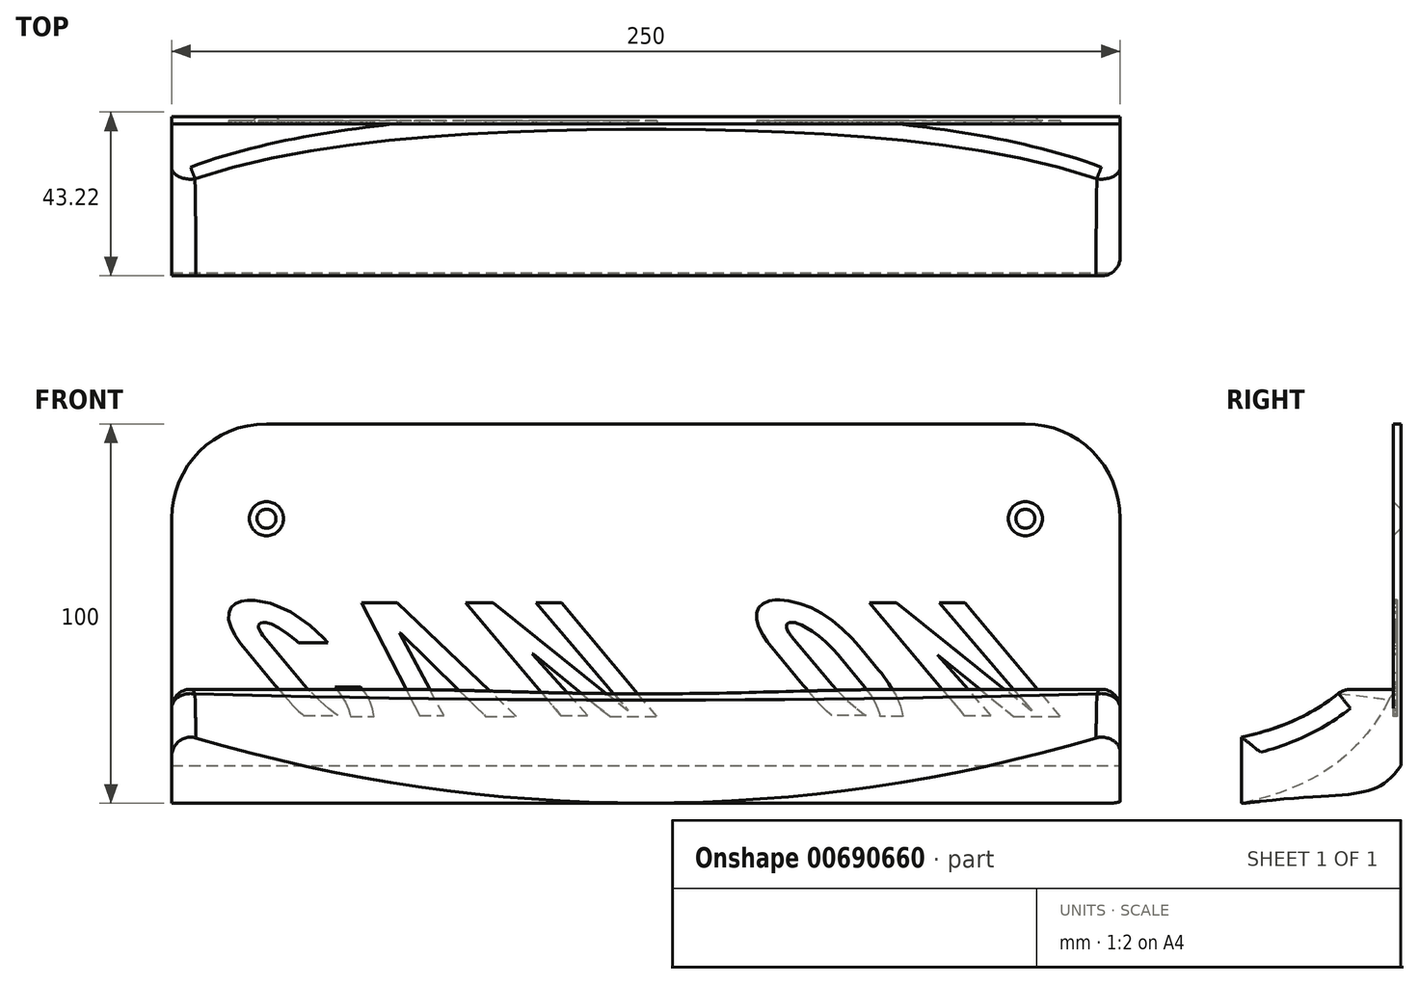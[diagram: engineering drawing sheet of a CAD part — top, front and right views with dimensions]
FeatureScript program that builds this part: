
annotation { "Feature Type Name" : "Feature", "Feature Type Description" : "" }
export const myFeature = defineFeature(function(context is Context, id is Id, definition is map)
    precondition{}
    {
        {
            assignVariable(context, id + "F0", {"name" : "raddurchmesser", "anyValue" : 736});
        }
        {
            var Q0;
            Q0=qCreatedBy(makeId("Front.planeOp"),FACE);
            var sketch = newSketch(context, id + "F1", { "sketchPlane" : qUnion([Q0])});
            skLineSegment(sketch, "E0.bottom", {"start": v(125, -50) * mm, "end": v(-125, -50) * mm});
            skLineSegment(sketch, "E0.top", {"start": v(100, 50) * mm, "end": v(-100, 50) * mm});
            skLineSegment(sketch, "E0.left", {"start": v(125, -50) * mm, "end": v(125, 25) * mm});
            skLineSegment(sketch, "E0.right", {"start": v(-125, -50) * mm, "end": v(-125, 25) * mm});
            skPoint(sketch, "E0.middle", {"position": v(0, 0) * mm});
            skPoint(sketch, "E1.visualSharp", {"position": v(-125, 50) * mm});
            skArc(sketch, "E1.filletArc", {"start": v(-100, 50) * mm, "mid": v(-117.68, 42.68) * mm, "end": v(-125, 25) * mm});
            skPoint(sketch, "E2.visualSharp", {"position": v(125, 50) * mm});
            skArc(sketch, "E2.filletArc", {"start": v(125, 25) * mm, "mid": v(117.68, 42.68) * mm, "end": v(100, 50) * mm});
            skSolve(sketch);
        }
        {
            var Q0;
            Q0=makeQuery(id+"F1.imprint","IMPRINT",FACE,{"disambiguationData":[TD([[makeQuery(id+"F1.imprint","IMPRINT",EDGE,{"derivedFrom":sQuery(id+"F1.wireOp",EDGE,"E0.bottom")}),-1.0]])]});
            extrude(context, id + "F2", {"entities" : qUnion([Q0]), "depth" : 2 * mm, "offsetDistance" : 25 * mm});
        }
        {
            var Q0;
            Q0=makeQuery(id+"F2.opExtrude","CAP_FACE",FACE,{"disambiguationData":[OSD([sQuery(id+"F1.wireOp",EDGE,"E0.bottom"),sQuery(id+"F1.wireOp",EDGE,"E0.top"),sQuery(id+"F1.wireOp",EDGE,"E0.left"),sQuery(id+"F1.wireOp",EDGE,"E0.right"),sQuery(id+"F1.wireOp",EDGE,"E1.filletArc"),sQuery(id+"F1.wireOp",EDGE,"E2.filletArc")])],"isStart":false});
            var sketch = newSketch(context, id + "F3", { "sketchPlane" : qUnion([Q0])});
            skPoint(sketch, "E3", {"position": v(-100, 25) * mm});
            skPoint(sketch, "E4", {"position": v(100, 25) * mm});
            skSolve(sketch);
        }
        {
            var Q0;
            Q0=sQuery(id+"F3.wireOp",VERTEX,"E3");
            var Q1;
            Q1=sQuery(id+"F3.wireOp",VERTEX,"E4");
            var Q2;
            Q2=makeQuery(id+"F2.opExtrude","SWEPT_BODY",BODY,{"disambiguationData":[OSD([sQuery(id+"F1.wireOp",EDGE,"E0.bottom"),sQuery(id+"F1.wireOp",EDGE,"E0.top"),sQuery(id+"F1.wireOp",EDGE,"E0.left"),sQuery(id+"F1.wireOp",EDGE,"E0.right"),sQuery(id+"F1.wireOp",EDGE,"E1.filletArc"),sQuery(id+"F1.wireOp",EDGE,"E2.filletArc")])]});
            hole(context, id + "F4", {"style" : HoleStyle.C_SINK, "endStyle" : HoleEndStyle.THROUGH, "holeDiameter" : 4 * mm, "cSinkDiameter" : 9 * mm, "cSinkAngle" : 90 * degree, "majorDiameter" : 5 * mm, "isTappedThrough" : true, "tappedDepth" : 12 * mm, "tapClearance" : 3, "locations" : qUnion([Q0, Q1]), "scope" : qUnion([Q2])});
        }
        {
            var Q0;
            Q0=makeQuery(id+"F2.opExtrude","CAP_FACE",FACE,{"disambiguationData":[OSD([sQuery(id+"F1.wireOp",EDGE,"E0.bottom"),sQuery(id+"F1.wireOp",EDGE,"E0.top"),sQuery(id+"F1.wireOp",EDGE,"E0.left"),sQuery(id+"F1.wireOp",EDGE,"E0.right")])],"isStart":false});
            var sketch = newSketch(context, id + "F5", { "sketchPlane" : qUnion([Q0])});
            skLineSegment(sketch, "E5.bottom", {"start": v(-125, -50) * mm, "end": v(125, -50) * mm});
            skLineSegment(sketch, "E5.top", {"start": v(-125, -20) * mm, "end": v(125, -20) * mm});
            skLineSegment(sketch, "E5.left", {"start": v(-125, -50) * mm, "end": v(-125, -20) * mm});
            skLineSegment(sketch, "E5.right", {"start": v(125, -50) * mm, "end": v(125, -20) * mm});
            skSolve(sketch);
        }
        {
            var Q0;
            Q0=makeQuery(id+"F5.imprint","IMPRINT",FACE,{"disambiguationData":[TD([[makeQuery(id+"F5.imprint","IMPRINT",EDGE,{"derivedFrom":sQuery(id+"F5.wireOp",EDGE,"E5.bottom")}),-1.0]])]});
            extrude(context, id + "F6", {"entities" : qUnion([Q0]), "operationType" : NewBodyOperationType.ADD, "depth" : 40 * mm, "offsetDistance" : 25 * mm});
        }
        {
            var Q0;
            Q0=makeQuery(id+"F2.opExtrude","CAP_FACE",FACE,{"disambiguationData":[OSD([sQuery(id+"F1.wireOp",EDGE,"E0.bottom"),sQuery(id+"F1.wireOp",EDGE,"E0.top"),sQuery(id+"F1.wireOp",EDGE,"E0.left"),sQuery(id+"F1.wireOp",EDGE,"E0.right"),sQuery(id+"F1.wireOp",EDGE,"E1.filletArc"),sQuery(id+"F1.wireOp",EDGE,"E2.filletArc")])],"isStart":false});
            var sketch = newSketch(context, id + "F7", { "sketchPlane" : qUnion([Q0])});
            skLineSegment(sketch, "E6", {"start": v(-104.56, 3.5) * mm, "end": v(-105.1, 3.5) * mm});
            skLineSegment(sketch, "E7", {"start": v(-105.1, 3.5) * mm, "end": v(-106.67, 3.27) * mm});
            skLineSegment(sketch, "E8", {"start": v(-106.67, 3.27) * mm, "end": v(-108.27, 2.6) * mm});
            skLineSegment(sketch, "E9", {"start": v(-108.27, 2.6) * mm, "end": v(-109.36, 1.52) * mm});
            skLineSegment(sketch, "E10", {"start": v(-109.36, 1.52) * mm, "end": v(-109.92, 0.11) * mm});
            skLineSegment(sketch, "E11", {"start": v(-109.92, 0.11) * mm, "end": v(-109.94, -1.6) * mm});
            skLineSegment(sketch, "E12", {"start": v(-109.94, -1.6) * mm, "end": v(-109.4, -3.57) * mm});
            skLineSegment(sketch, "E13", {"start": v(-109.4, -3.57) * mm, "end": v(-108.31, -5.75) * mm});
            skLineSegment(sketch, "E14", {"start": v(-108.31, -5.75) * mm, "end": v(-107.09, -7.53) * mm});
            skLineSegment(sketch, "E15", {"start": v(-107.09, -7.53) * mm, "end": v(-106.63, -8.08) * mm});
            skLineSegment(sketch, "E16", {"start": v(-106.63, -8.08) * mm, "end": v(-97.74, -18.87) * mm});
            skLineSegment(sketch, "E17", {"start": v(-97.74, -18.87) * mm, "end": v(-97.17, -19.56) * mm});
            skLineSegment(sketch, "E18", {"start": v(-97.17, -19.56) * mm, "end": v(-95.4, -21.6) * mm});
            skLineSegment(sketch, "E19", {"start": v(-95.4, -21.6) * mm, "end": v(-93.3, -23.92) * mm});
            skLineSegment(sketch, "E20", {"start": v(-93.3, -23.92) * mm, "end": v(-91.54, -25.7) * mm});
            skLineSegment(sketch, "E21", {"start": v(-91.54, -25.7) * mm, "end": v(-90.6, -26.57) * mm});
            skLineSegment(sketch, "E22", {"start": v(-90.6, -26.57) * mm, "end": v(-90.28, -26.83) * mm});
            skLineSegment(sketch, "E23", {"start": v(-90.28, -26.83) * mm, "end": v(-90.27, -26.84) * mm});
            skLineSegment(sketch, "E24", {"start": v(-90.27, -26.84) * mm, "end": v(-90.18, -26.87) * mm});
            skLineSegment(sketch, "E25", {"start": v(-90.18, -26.87) * mm, "end": v(-90.15, -26.87) * mm});
            skLineSegment(sketch, "E26", {"start": v(-90.15, -26.87) * mm, "end": v(-81.14, -26.87) * mm});
            skLineSegment(sketch, "E27", {"start": v(-81.14, -26.87) * mm, "end": v(-81.77, -26.47) * mm});
            skLineSegment(sketch, "E28", {"start": v(-81.77, -26.47) * mm, "end": v(-83.55, -25.11) * mm});
            skLineSegment(sketch, "E29", {"start": v(-83.55, -25.11) * mm, "end": v(-86.05, -22.95) * mm});
            skLineSegment(sketch, "E30", {"start": v(-86.05, -22.95) * mm, "end": v(-88.48, -20.56) * mm});
            skLineSegment(sketch, "E31", {"start": v(-88.48, -20.56) * mm, "end": v(-90.15, -18.76) * mm});
            skLineSegment(sketch, "E32", {"start": v(-90.15, -18.76) * mm, "end": v(-90.68, -18.14) * mm});
            skLineSegment(sketch, "E33", {"start": v(-90.68, -18.14) * mm, "end": v(-100.73, -6.07) * mm});
            skLineSegment(sketch, "E34", {"start": v(-100.73, -6.07) * mm, "end": v(-100.92, -5.85) * mm});
            skLineSegment(sketch, "E35", {"start": v(-100.92, -5.85) * mm, "end": v(-101.42, -5.15) * mm});
            skLineSegment(sketch, "E36", {"start": v(-101.42, -5.15) * mm, "end": v(-101.88, -4.35) * mm});
            skLineSegment(sketch, "E37", {"start": v(-101.88, -4.35) * mm, "end": v(-102.1, -3.68) * mm});
            skLineSegment(sketch, "E38", {"start": v(-102.1, -3.68) * mm, "end": v(-102.12, -3.14) * mm});
            skLineSegment(sketch, "E39", {"start": v(-102.12, -3.14) * mm, "end": v(-101.91, -2.73) * mm});
            skLineSegment(sketch, "E40", {"start": v(-101.91, -2.73) * mm, "end": v(-101.5, -2.47) * mm});
            skLineSegment(sketch, "E41", {"start": v(-101.5, -2.47) * mm, "end": v(-100.87, -2.37) * mm});
            skLineSegment(sketch, "E42", {"start": v(-100.87, -2.37) * mm, "end": v(-100.24, -2.38) * mm});
            skLineSegment(sketch, "E43", {"start": v(-100.24, -2.38) * mm, "end": v(-100.04, -2.41) * mm});
            skLineSegment(sketch, "E44", {"start": v(-100.04, -2.41) * mm, "end": v(-99.72, -2.45) * mm});
            skLineSegment(sketch, "E45", {"start": v(-99.72, -2.45) * mm, "end": v(-98.72, -2.83) * mm});
            skLineSegment(sketch, "E46", {"start": v(-98.72, -2.83) * mm, "end": v(-96.75, -3.83) * mm});
            skLineSegment(sketch, "E47", {"start": v(-96.75, -3.83) * mm, "end": v(-94.3, -5.45) * mm});
            skLineSegment(sketch, "E48", {"start": v(-94.3, -5.45) * mm, "end": v(-92.22, -7.13) * mm});
            skLineSegment(sketch, "E49", {"start": v(-92.22, -7.13) * mm, "end": v(-91.57, -7.73) * mm});
            skLineSegment(sketch, "E50", {"start": v(-91.57, -7.73) * mm, "end": v(-83.82, -7.73) * mm});
            skLineSegment(sketch, "E51", {"start": v(-83.82, -7.73) * mm, "end": v(-84.92, -6.5) * mm});
            skLineSegment(sketch, "E52", {"start": v(-84.92, -6.5) * mm, "end": v(-88.54, -3.1) * mm});
            skLineSegment(sketch, "E53", {"start": v(-88.54, -3.1) * mm, "end": v(-93.6, 0.44) * mm});
            skLineSegment(sketch, "E54", {"start": v(-93.6, 0.44) * mm, "end": v(-98.95, 2.7) * mm});
            skLineSegment(sketch, "E55", {"start": v(-98.95, 2.7) * mm, "end": v(-103.16, 3.5) * mm});
            skLineSegment(sketch, "E56", {"start": v(-103.16, 3.5) * mm, "end": v(-104.56, 3.5) * mm});
            skLineSegment(sketch, "E57", {"start": v(-77.84, -27.12) * mm, "end": v(-71.65, -27.12) * mm});
            skLineSegment(sketch, "E58", {"start": v(-71.65, -27.12) * mm, "end": v(-71.7, -26.65) * mm});
            skLineSegment(sketch, "E59", {"start": v(-71.7, -26.65) * mm, "end": v(-72.02, -25.28) * mm});
            skLineSegment(sketch, "E60", {"start": v(-72.02, -25.28) * mm, "end": v(-72.7, -23.34) * mm});
            skLineSegment(sketch, "E61", {"start": v(-72.7, -23.34) * mm, "end": v(-73.73, -21.36) * mm});
            skLineSegment(sketch, "E62", {"start": v(-73.73, -21.36) * mm, "end": v(-74.75, -19.86) * mm});
            skLineSegment(sketch, "E63", {"start": v(-74.75, -19.86) * mm, "end": v(-75.14, -19.4) * mm});
            skLineSegment(sketch, "E64", {"start": v(-75.14, -19.4) * mm, "end": v(-81.95, -19.4) * mm});
            skLineSegment(sketch, "E65", {"start": v(-81.95, -19.4) * mm, "end": v(-81.53, -19.9) * mm});
            skLineSegment(sketch, "E66", {"start": v(-81.53, -19.9) * mm, "end": v(-80.35, -21.5) * mm});
            skLineSegment(sketch, "E67", {"start": v(-80.35, -21.5) * mm, "end": v(-79.19, -23.43) * mm});
            skLineSegment(sketch, "E68", {"start": v(-79.19, -23.43) * mm, "end": v(-78.37, -25.28) * mm});
            skLineSegment(sketch, "E69", {"start": v(-78.37, -25.28) * mm, "end": v(-77.95, -26.65) * mm});
            skLineSegment(sketch, "E70", {"start": v(-77.95, -26.65) * mm, "end": v(-77.84, -27.12) * mm});
            skLineSegment(sketch, "E71", {"start": v(26.03, -18.8) * mm, "end": v(16.1, 2.89) * mm});
            skLineSegment(sketch, "E72", {"start": v(16.1, 2.89) * mm, "end": v(9.93, 2.89) * mm});
            skLineSegment(sketch, "E73", {"start": v(9.93, 2.89) * mm, "end": v(17.34, -11.96) * mm});
            skLineSegment(sketch, "E74", {"start": v(17.34, -11.96) * mm, "end": v(17.13, -11.96) * mm});
            skLineSegment(sketch, "E75", {"start": v(17.13, -11.96) * mm, "end": v(-2.65, 2.89) * mm});
            skLineSegment(sketch, "E76", {"start": v(-2.65, 2.89) * mm, "end": v(-11.42, 2.89) * mm});
            skLineSegment(sketch, "E77", {"start": v(-11.42, 2.89) * mm, "end": v(19.58, -20.05) * mm});
            skLineSegment(sketch, "E78", {"start": v(19.58, -20.05) * mm, "end": v(25.54, -27.11) * mm});
            skLineSegment(sketch, "E79", {"start": v(25.54, -27.11) * mm, "end": v(33.04, -27.11) * mm});
            skLineSegment(sketch, "E80", {"start": v(33.04, -27.11) * mm, "end": v(26.03, -18.8) * mm});
            skLineSegment(sketch, "E81", {"start": v(-28.98, 2.89) * mm, "end": v(-4.66, -25.6) * mm});
            skLineSegment(sketch, "E82", {"start": v(-4.66, -25.6) * mm, "end": v(-4.87, -25.6) * mm});
            skLineSegment(sketch, "E83", {"start": v(-4.87, -25.6) * mm, "end": v(-40.28, 2.89) * mm});
            skLineSegment(sketch, "E84", {"start": v(-40.28, 2.89) * mm, "end": v(-47.46, 2.89) * mm});
            skLineSegment(sketch, "E85", {"start": v(-47.46, 2.89) * mm, "end": v(-22.5, -26.86) * mm});
            skLineSegment(sketch, "E86", {"start": v(-22.5, -26.86) * mm, "end": v(-15.37, -26.86) * mm});
            skLineSegment(sketch, "E87", {"start": v(-15.37, -26.86) * mm, "end": v(-29.96, -10.7) * mm});
            skLineSegment(sketch, "E88", {"start": v(-29.96, -10.7) * mm, "end": v(-29.76, -10.7) * mm});
            skLineSegment(sketch, "E89", {"start": v(-29.76, -10.7) * mm, "end": v(-9.52, -27.11) * mm});
            skLineSegment(sketch, "E90", {"start": v(-9.52, -27.11) * mm, "end": v(2.87, -27.11) * mm});
            skLineSegment(sketch, "E91", {"start": v(2.87, -27.11) * mm, "end": v(-22.3, 2.89) * mm});
            skLineSegment(sketch, "E92", {"start": v(-22.3, 2.89) * mm, "end": v(-28.98, 2.89) * mm});
            skLineSegment(sketch, "E93", {"start": v(77.38, 2.89) * mm, "end": v(101.7, -25.6) * mm});
            skLineSegment(sketch, "E94", {"start": v(101.7, -25.6) * mm, "end": v(101.5, -25.6) * mm});
            skLineSegment(sketch, "E95", {"start": v(101.5, -25.6) * mm, "end": v(66.07, 2.89) * mm});
            skLineSegment(sketch, "E96", {"start": v(66.07, 2.89) * mm, "end": v(58.9, 2.89) * mm});
            skLineSegment(sketch, "E97", {"start": v(58.9, 2.89) * mm, "end": v(83.86, -26.86) * mm});
            skLineSegment(sketch, "E98", {"start": v(83.86, -26.86) * mm, "end": v(90.99, -26.86) * mm});
            skLineSegment(sketch, "E99", {"start": v(90.99, -26.86) * mm, "end": v(76.66, -10.7) * mm});
            skLineSegment(sketch, "E100", {"start": v(76.66, -10.7) * mm, "end": v(76.6, -10.7) * mm});
            skLineSegment(sketch, "E101", {"start": v(76.6, -10.7) * mm, "end": v(96.84, -27.11) * mm});
            skLineSegment(sketch, "E102", {"start": v(96.84, -27.11) * mm, "end": v(109.23, -27.11) * mm});
            skLineSegment(sketch, "E103", {"start": v(109.23, -27.11) * mm, "end": v(84.06, 2.89) * mm});
            skLineSegment(sketch, "E104", {"start": v(84.06, 2.89) * mm, "end": v(77.38, 2.89) * mm});
            skLineSegment(sketch, "E105", {"start": v(-75, 2.89) * mm, "end": v(-59.66, -26.86) * mm});
            skLineSegment(sketch, "E106", {"start": v(-59.66, -26.86) * mm, "end": v(-53.28, -26.86) * mm});
            skLineSegment(sketch, "E107", {"start": v(-53.28, -26.86) * mm, "end": v(-64.91, -5.16) * mm});
            skLineSegment(sketch, "E108", {"start": v(-64.91, -5.16) * mm, "end": v(-64.72, -5.16) * mm});
            skLineSegment(sketch, "E109", {"start": v(-64.72, -5.16) * mm, "end": v(-42.25, -27.11) * mm});
            skLineSegment(sketch, "E110", {"start": v(-42.25, -27.11) * mm, "end": v(-34.2, -27.11) * mm});
            skLineSegment(sketch, "E111", {"start": v(-34.2, -27.11) * mm, "end": v(-65.58, 2.89) * mm});
            skLineSegment(sketch, "E112", {"start": v(-65.58, 2.89) * mm, "end": v(-75, 2.89) * mm});
            skLineSegment(sketch, "E113", {"start": v(48.47, -18.12) * mm, "end": v(49, -18.74) * mm});
            skLineSegment(sketch, "E114", {"start": v(49, -18.74) * mm, "end": v(50.68, -20.55) * mm});
            skLineSegment(sketch, "E115", {"start": v(50.68, -20.55) * mm, "end": v(53.11, -22.94) * mm});
            skLineSegment(sketch, "E116", {"start": v(53.11, -22.94) * mm, "end": v(55.61, -25.1) * mm});
            skLineSegment(sketch, "E117", {"start": v(55.61, -25.1) * mm, "end": v(57.4, -26.46) * mm});
            skLineSegment(sketch, "E118", {"start": v(57.4, -26.46) * mm, "end": v(58.03, -26.86) * mm});
            skLineSegment(sketch, "E119", {"start": v(58.03, -26.86) * mm, "end": v(49, -26.86) * mm});
            skLineSegment(sketch, "E120", {"start": v(49, -26.86) * mm, "end": v(48.97, -26.86) * mm});
            skLineSegment(sketch, "E121", {"start": v(48.97, -26.86) * mm, "end": v(48.88, -26.83) * mm});
            skLineSegment(sketch, "E122", {"start": v(48.88, -26.83) * mm, "end": v(48.88, -26.82) * mm});
            skLineSegment(sketch, "E123", {"start": v(48.88, -26.82) * mm, "end": v(48.55, -26.57) * mm});
            skLineSegment(sketch, "E124", {"start": v(48.55, -26.57) * mm, "end": v(47.6, -25.69) * mm});
            skLineSegment(sketch, "E125", {"start": v(47.6, -25.69) * mm, "end": v(45.85, -23.91) * mm});
            skLineSegment(sketch, "E126", {"start": v(45.85, -23.91) * mm, "end": v(43.74, -21.6) * mm});
            skLineSegment(sketch, "E127", {"start": v(43.74, -21.6) * mm, "end": v(41.98, -19.55) * mm});
            skLineSegment(sketch, "E128", {"start": v(41.98, -19.55) * mm, "end": v(41.4, -18.85) * mm});
            skLineSegment(sketch, "E129", {"start": v(41.4, -18.85) * mm, "end": v(32.5, -8.06) * mm});
            skLineSegment(sketch, "E130", {"start": v(32.5, -8.06) * mm, "end": v(32.04, -7.5) * mm});
            skLineSegment(sketch, "E131", {"start": v(32.04, -7.5) * mm, "end": v(30.82, -5.72) * mm});
            skLineSegment(sketch, "E132", {"start": v(30.82, -5.72) * mm, "end": v(29.72, -3.54) * mm});
            skLineSegment(sketch, "E133", {"start": v(29.72, -3.54) * mm, "end": v(29.18, -1.57) * mm});
            skLineSegment(sketch, "E134", {"start": v(29.18, -1.57) * mm, "end": v(29.2, 0.15) * mm});
            skLineSegment(sketch, "E135", {"start": v(29.2, 0.15) * mm, "end": v(29.76, 1.56) * mm});
            skLineSegment(sketch, "E136", {"start": v(29.76, 1.56) * mm, "end": v(30.85, 2.63) * mm});
            skLineSegment(sketch, "E137", {"start": v(30.85, 2.63) * mm, "end": v(32.46, 3.3) * mm});
            skLineSegment(sketch, "E138", {"start": v(32.46, 3.3) * mm, "end": v(34.04, 3.54) * mm});
            skLineSegment(sketch, "E139", {"start": v(34.04, 3.54) * mm, "end": v(34.57, 3.54) * mm});
            skLineSegment(sketch, "E140", {"start": v(34.57, 3.54) * mm, "end": v(35.33, 3.54) * mm});
            skLineSegment(sketch, "E141", {"start": v(35.33, 3.54) * mm, "end": v(37.62, 3.3) * mm});
            skLineSegment(sketch, "E142", {"start": v(37.62, 3.3) * mm, "end": v(40.6, 2.62) * mm});
            skLineSegment(sketch, "E143", {"start": v(40.6, 2.62) * mm, "end": v(43.52, 1.51) * mm});
            skLineSegment(sketch, "E144", {"start": v(43.52, 1.51) * mm, "end": v(46.35, 0) * mm});
            skLineSegment(sketch, "E145", {"start": v(46.35, 0) * mm, "end": v(49.1, -1.85) * mm});
            skLineSegment(sketch, "E146", {"start": v(49.1, -1.85) * mm, "end": v(51.74, -4.05) * mm});
            skLineSegment(sketch, "E147", {"start": v(51.74, -4.05) * mm, "end": v(54.28, -6.55) * mm});
            skLineSegment(sketch, "E148", {"start": v(54.28, -6.55) * mm, "end": v(56.14, -8.6) * mm});
            skLineSegment(sketch, "E149", {"start": v(56.14, -8.6) * mm, "end": v(56.72, -9.32) * mm});
            skLineSegment(sketch, "E150", {"start": v(56.72, -9.32) * mm, "end": v(61.31, -14.9) * mm});
            skLineSegment(sketch, "E151", {"start": v(61.31, -14.9) * mm, "end": v(62.03, -15.78) * mm});
            skLineSegment(sketch, "E152", {"start": v(62.03, -15.78) * mm, "end": v(64.05, -18.52) * mm});
            skLineSegment(sketch, "E153", {"start": v(64.05, -18.52) * mm, "end": v(65.88, -21.62) * mm});
            skLineSegment(sketch, "E154", {"start": v(65.88, -21.62) * mm, "end": v(67, -24.4) * mm});
            skLineSegment(sketch, "E155", {"start": v(67, -24.4) * mm, "end": v(67.54, -26.43) * mm});
            skLineSegment(sketch, "E156", {"start": v(67.54, -26.43) * mm, "end": v(67.66, -27.11) * mm});
            skLineSegment(sketch, "E157", {"start": v(67.66, -27.11) * mm, "end": v(61.76, -27.11) * mm});
            skLineSegment(sketch, "E158", {"start": v(61.76, -27.11) * mm, "end": v(61.66, -26.65) * mm});
            skLineSegment(sketch, "E159", {"start": v(61.66, -26.65) * mm, "end": v(61.23, -25.27) * mm});
            skLineSegment(sketch, "E160", {"start": v(61.23, -25.27) * mm, "end": v(60.41, -23.42) * mm});
            skLineSegment(sketch, "E161", {"start": v(60.41, -23.42) * mm, "end": v(59.25, -21.5) * mm});
            skLineSegment(sketch, "E162", {"start": v(59.25, -21.5) * mm, "end": v(58.07, -19.9) * mm});
            skLineSegment(sketch, "E163", {"start": v(58.07, -19.9) * mm, "end": v(57.65, -19.39) * mm});
            skLineSegment(sketch, "E164", {"start": v(57.65, -19.39) * mm, "end": v(51.14, -11.47) * mm});
            skLineSegment(sketch, "E165", {"start": v(51.14, -11.47) * mm, "end": v(50.7, -10.92) * mm});
            skLineSegment(sketch, "E166", {"start": v(50.7, -10.92) * mm, "end": v(49.26, -9.34) * mm});
            skLineSegment(sketch, "E167", {"start": v(49.26, -9.34) * mm, "end": v(47.38, -7.52) * mm});
            skLineSegment(sketch, "E168", {"start": v(47.38, -7.52) * mm, "end": v(45.57, -5.98) * mm});
            skLineSegment(sketch, "E169", {"start": v(45.57, -5.98) * mm, "end": v(43.86, -4.73) * mm});
            skLineSegment(sketch, "E170", {"start": v(43.86, -4.73) * mm, "end": v(42.31, -3.75) * mm});
            skLineSegment(sketch, "E171", {"start": v(42.31, -3.75) * mm, "end": v(40.97, -3.04) * mm});
            skLineSegment(sketch, "E172", {"start": v(40.97, -3.04) * mm, "end": v(39.88, -2.59) * mm});
            skLineSegment(sketch, "E173", {"start": v(39.88, -2.59) * mm, "end": v(39.3, -2.4) * mm});
            skLineSegment(sketch, "E174", {"start": v(39.3, -2.4) * mm, "end": v(39.1, -2.38) * mm});
            skLineSegment(sketch, "E175", {"start": v(39.1, -2.38) * mm, "end": v(38.9, -2.35) * mm});
            skLineSegment(sketch, "E176", {"start": v(38.9, -2.35) * mm, "end": v(38.27, -2.33) * mm});
            skLineSegment(sketch, "E177", {"start": v(38.27, -2.33) * mm, "end": v(37.64, -2.44) * mm});
            skLineSegment(sketch, "E178", {"start": v(37.64, -2.44) * mm, "end": v(37.22, -2.7) * mm});
            skLineSegment(sketch, "E179", {"start": v(37.22, -2.7) * mm, "end": v(37.02, -3.1) * mm});
            skLineSegment(sketch, "E180", {"start": v(37.02, -3.1) * mm, "end": v(37.03, -3.65) * mm});
            skLineSegment(sketch, "E181", {"start": v(37.03, -3.65) * mm, "end": v(37.26, -4.32) * mm});
            skLineSegment(sketch, "E182", {"start": v(37.26, -4.32) * mm, "end": v(37.72, -5.12) * mm});
            skLineSegment(sketch, "E183", {"start": v(37.72, -5.12) * mm, "end": v(38.22, -5.82) * mm});
            skLineSegment(sketch, "E184", {"start": v(38.22, -5.82) * mm, "end": v(38.4, -6.04) * mm});
            skLineSegment(sketch, "E185", {"start": v(38.4, -6.04) * mm, "end": v(48.47, -18.12) * mm});
            skSolve(sketch);
        }
        {
            var Q0;
            Q0 = qSketchRegion(id + "F7", true);
            extrude(context, id + "F8", {"entities" : qUnion([Q0]), "operationType" : NewBodyOperationType.REMOVE, "oppositeDirection" : true, "depth" : 1 * mm, "offsetDistance" : 25 * mm});
        }
        {
            var Q0;
            Q0=qCreatedBy(makeId("Top.planeOp"),FACE);
            cPlane(context, id + "F9", {"entities" : qUnion([Q0]), "cplaneType" : CPlaneType.OFFSET, "offset" : (getVariable(context, 'raddurchmesser') / 2) * mm, "width" : 150 * mm, "height" : 150 * mm});
        }
        {
            var Q0;
            Q0=qCreatedBy(makeId("Right.planeOp"),FACE);
            var sketch = newSketch(context, id + "F10", { "sketchPlane" : qUnion([Q0])});
            skFitSpline(sketch, "E186", {"points": [v(-2, -20) * mm, v(-42, -50) * mm], "startDerivative": vector(-17.75, -42.6) * mm, "endDerivative": vector(-65.6, -13.42) * mm});
            skLineSegment(sketch, "E187", {"start": v(-42, -50) * mm, "end": v(-42, -20) * mm});
            skLineSegment(sketch, "E188", {"start": v(-42, -20) * mm, "end": v(-2, -20) * mm});
            skSolve(sketch);
        }
        {
            var Q0;
            Q0=qCreatedBy(id+"F9.planeOp",FACE);
            var sketch = newSketch(context, id + "F11", { "sketchPlane" : qUnion([Q0])});
            skLineSegment(sketch, "E189", {"start": v(0, 55.44) * mm, "end": v(0, -46.61) * mm, "construction": true});
            skSolve(sketch);
        }
        {
            var Q0;
            Q0 = qSketchRegion(id + "F10", true);
            var Q1;
            Q1=sQuery(id+"F11.wireOp",EDGE,"E189");
            revolve(context, id + "F12", {"operationType" : NewBodyOperationType.REMOVE, "surfaceOperationType" : NewSurfaceOperationType.NEW, "entities" : qUnion([Q0]), "axis" : qUnion([Q1]), "revolveType" : RevolveType.FULL, "oppositeDirection" : true});
        }
        {
            var Q0;
            Q0=makeQuery(id+"F6.boolean.opBoolean","MERGE",FACE,{"derivedFrom":[makeQuery(id+"F2.opExtrude","SWEPT_FACE",FACE,{"disambiguationData":[OSD([sQuery(id+"F1.wireOp",EDGE,"E0.left")])]}),makeQuery(id+"F6.opExtrude","SWEPT_FACE",FACE,{"disambiguationData":[OSD([sQuery(id+"F5.wireOp",EDGE,"E5.right")])]})]});
            var sketch = newSketch(context, id + "F13", { "sketchPlane" : qUnion([Q0])});
            skFitSpline(sketch, "E190", {"points": [v(0, -40.13) * mm, v(-41.18, -50) * mm], "startDerivative": vector(-21.89, -30.15) * mm, "endDerivative": vector(-85.9, -10.57) * mm});
            skLineSegment(sketch, "E191", {"start": v(0, -40.13) * mm, "end": v(0, -50) * mm});
            skLineSegment(sketch, "E192", {"start": v(0, -50) * mm, "end": v(-41.18, -50) * mm});
            skSolve(sketch);
        }
        {
            var Q0;
            Q0=makeQuery(id+"F13.imprint","IMPRINT",FACE,{"disambiguationData":[TD([[makeQuery(id+"F13.imprint","IMPRINT",EDGE,{"derivedFrom":sQuery(id+"F13.wireOp",EDGE,"E190")}),1.0]])]});
            extrude(context, id + "F14", {"entities" : qUnion([Q0]), "operationType" : NewBodyOperationType.REMOVE, "endBound" : BoundingType.UP_TO_NEXT, "oppositeDirection" : true, "depth" : 25 * mm, "offsetDistance" : 25 * mm});
        }
        {
            var Q0;
            Q0=makeQuery(id+"F14.boolean.opBoolean","COPY",EDGE,{"derivedFrom":makeQuery(id+"F14.opExtrude","SWEPT_EDGE",EDGE,{"disambiguationData":[OSD([sQuery(id+"F1.wireOp",EDGE,"E0.left"),sQuery(id+"F13.wireOp",EDGE,"E190"),sQuery(id+"F13.wireOp",EDGE,"E191")])]})});
            var Q1;
            Q1=makeQuery(id+"F14.boolean.opBoolean","COPY",EDGE,{"derivedFrom":makeQuery(id+"F14.opExtrude","CAP_EDGE",EDGE,{"disambiguationData":[OSD([sQuery(id+"F13.wireOp",EDGE,"E190")])],"isStart":true})});
            var Q2;
            Q2=makeQuery(id+"F6.opExtrude","CAP_EDGE",EDGE,{"disambiguationData":[OSD([sQuery(id+"F5.wireOp",EDGE,"E5.right")])],"isStart":false});
            var Q3;
            Q3=makeQuery(id+"F14.boolean.opBoolean","COPY",EDGE,{"derivedFrom":makeQuery(id+"F14.opExtrude","CAP_EDGE",EDGE,{"disambiguationData":[OSD([sQuery(id+"F13.wireOp",EDGE,"E190")])],"isStart":false})});
            var Q4;
            Q4=makeQuery(id+"F12.boolean.opBoolean","INTERSECT",EDGE,{"derivedFrom":[makeQuery(id+"F6.boolean.opBoolean","MERGE",FACE,{"derivedFrom":[makeQuery(id+"F2.opExtrude","SWEPT_FACE",FACE,{"disambiguationData":[OSD([sQuery(id+"F1.wireOp",EDGE,"E0.right")])]}),makeQuery(id+"F6.opExtrude","SWEPT_FACE",FACE,{"disambiguationData":[OSD([sQuery(id+"F5.wireOp",EDGE,"E5.left")])]})]}),makeQuery(id+"F12.opRevolve","SWEPT_FACE",FACE,{"disambiguationData":[OSD([sQuery(id+"F10.wireOp",EDGE,"E186")])]})]});
            var Q5;
            Q5=makeQuery(id+"F12.boolean.opBoolean","INTERSECT",EDGE,{"derivedFrom":[makeQuery(id+"F6.boolean.opBoolean","MERGE",FACE,{"derivedFrom":[makeQuery(id+"F2.opExtrude","SWEPT_FACE",FACE,{"disambiguationData":[OSD([sQuery(id+"F1.wireOp",EDGE,"E0.left")])]}),makeQuery(id+"F6.opExtrude","SWEPT_FACE",FACE,{"disambiguationData":[OSD([sQuery(id+"F5.wireOp",EDGE,"E5.right")])]})]}),makeQuery(id+"F12.opRevolve","SWEPT_FACE",FACE,{"disambiguationData":[OSD([sQuery(id+"F10.wireOp",EDGE,"E186")])]})]});
            fillet(context, id + "F15", {"entities" : qUnion([Q0, Q1, Q2, Q3, Q4, Q5]), "radius" : 5 * mm, "tangentPropagation" : true, "allowEdgeOverflow" : false});
        }
        {
            var Q0;
            Q0=makeQuery(id+"F12.boolean.opBoolean","INTERSECT",EDGE,{"disambiguationData":[OD(1.0)],"derivedFrom":[makeQuery(id+"F6.opExtrude","SWEPT_FACE",FACE,{"disambiguationData":[OSD([sQuery(id+"F5.wireOp",EDGE,"E5.top")])]}),makeQuery(id+"F12.opRevolve","SWEPT_FACE",FACE,{"disambiguationData":[OSD([sQuery(id+"F10.wireOp",EDGE,"E186")])]})]});
            fillet(context, id + "F16", {"entities" : qUnion([Q0]), "radius" : 5 * mm, "tangentPropagation" : true, "allowEdgeOverflow" : false});
        }
    });
